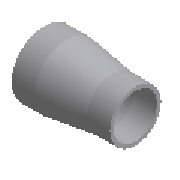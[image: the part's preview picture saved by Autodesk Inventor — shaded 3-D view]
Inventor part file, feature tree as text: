
AUTODESK INVENTOR PART (.ipt)
format: ipt  version: 2025.1 (Build 291241020, 241B)  size: 163,840 bytes
history: native  units: mm (DEFAULTED — no unit token found)
features: other x4, revolve x1
ambient origin geometry x8: Origin, YZ Plane, XZ Plane, XY Plane, X Axis, Y Axis, Z Axis, Center Point
bodies: Solid1 (feature_tree)
feature tree (5):
  revolve  "Revolution1"  [1 undecoded]
  other  "Work Axis1"
  other  "Work Point1"
  other  "Work Axis2"
  other  "Work Point2"
note: 1 required parameter value undecoded (feature->parameter linkage not recoverable at this tier; creation-order binding heuristic only, values carry confidence <= 0.55)
